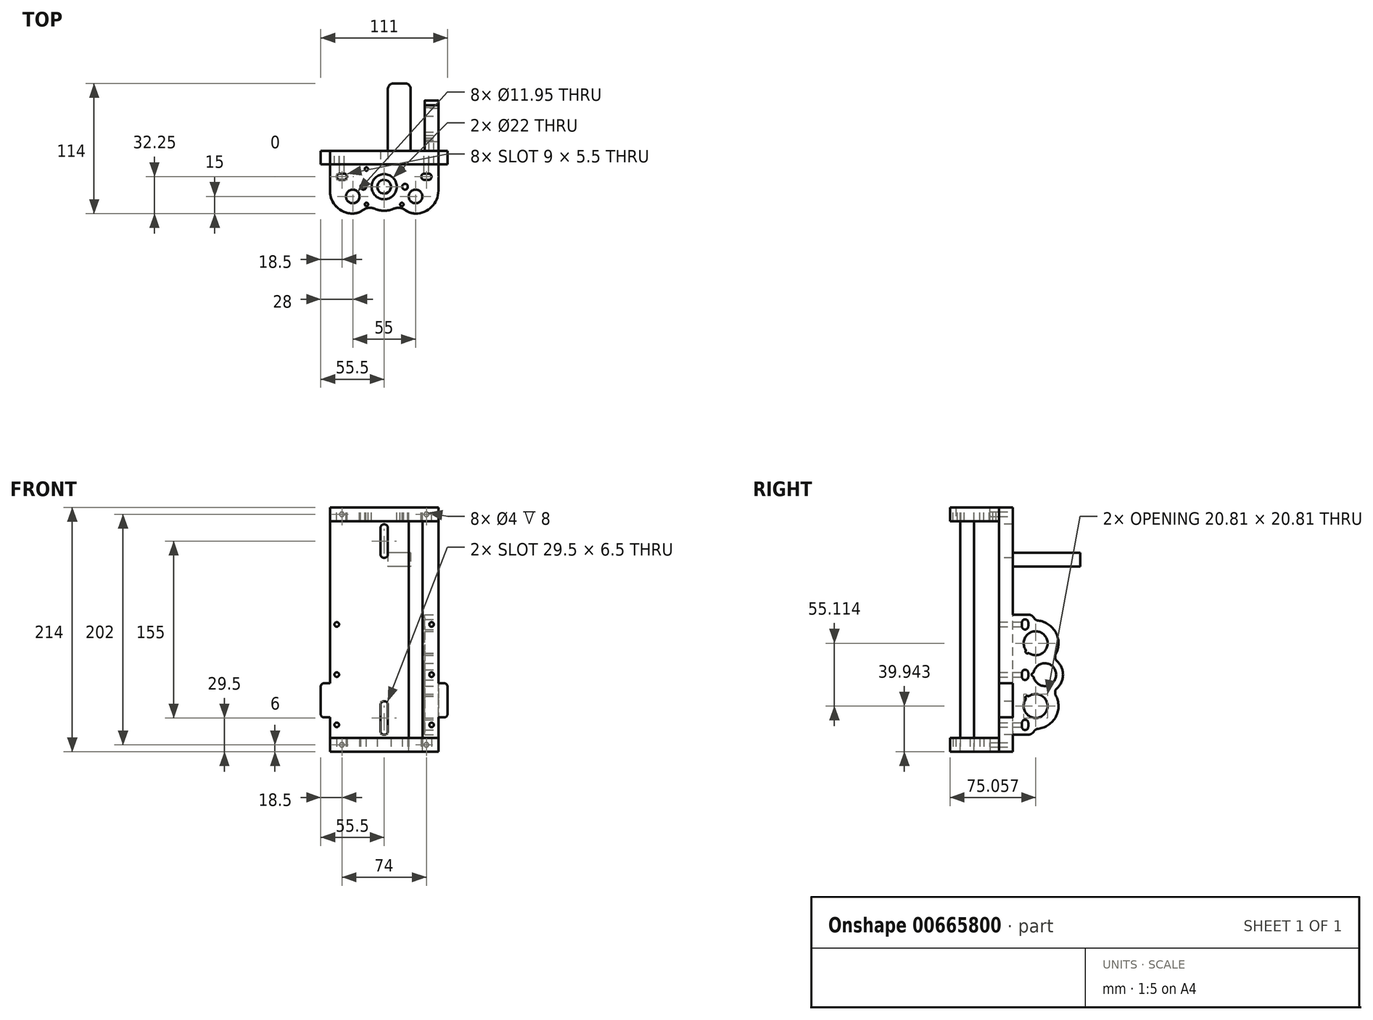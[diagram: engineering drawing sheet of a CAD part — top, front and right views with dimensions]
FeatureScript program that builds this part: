
annotation { "Feature Type Name" : "Feature", "Feature Type Description" : "" }
export const myFeature = defineFeature(function(context is Context, id is Id, definition is map)
    precondition{}
    {
        {
            assignVariable(context, id + "F0", {"name" : "L", "anyValue" : 214});
        }
        {
            var Q0;
            Q0=qCreatedBy(makeId("Front.planeOp"),FACE);
            var sketch = newSketch(context, id + "F1", { "sketchPlane" : qUnion([Q0])});
            skLineSegment(sketch, "E0.bottom", {"start": v(47.5, 0) * mm, "end": v(-47.5, 0) * mm});
            skLineSegment(sketch, "E0.top", {"start": v(-47.5, 214) * mm, "end": v(47.5, 214) * mm});
            skLineSegment(sketch, "E0.left", {"start": v(-47.5, 0) * mm, "end": v(-47.5, 214) * mm});
            skLineSegment(sketch, "E0.right", {"start": v(47.5, 0) * mm, "end": v(47.5, 214) * mm});
            skLineSegment(sketch, "E1.left", {"start": v(3.25, 196) * mm, "end": v(3.25, 173) * mm});
            skLineSegment(sketch, "E1.right", {"start": v(-3.25, 196) * mm, "end": v(-3.25, 173) * mm});
            skArc(sketch, "E2", {"start": v(3.25, 196) * mm, "mid": v(0, 199.25) * mm, "end": v(-3.25, 196) * mm});
            skArc(sketch, "E3", {"start": v(-3.25, 173) * mm, "mid": v(0, 169.75) * mm, "end": v(3.25, 173) * mm});
            skLineSegment(sketch, "E4", {"start": v(0, 214) * mm, "end": v(0, 196) * mm, "construction": true});
            skLineSegment(sketch, "E5.left", {"start": v(-3.25, 18) * mm, "end": v(-3.25, 41) * mm});
            skLineSegment(sketch, "E5.right", {"start": v(3.25, 18) * mm, "end": v(3.25, 41) * mm});
            skArc(sketch, "E6", {"start": v(-3.25, 18) * mm, "mid": v(0, 14.75) * mm, "end": v(3.25, 18) * mm});
            skArc(sketch, "E7", {"start": v(3.25, 41) * mm, "mid": v(0, 44.25) * mm, "end": v(-3.25, 41) * mm});
            skLineSegment(sketch, "E8", {"start": v(0, 0) * mm, "end": v(0, 18) * mm, "construction": true});
            skSolve(sketch);
        }
        {
            var Q0;
            Q0=qSketchRegion(id+"F1",true);
            extrude(context, id + "F2", {"entities" : qUnion([Q0]), "oppositeDirection" : true, "depth" : 12 * mm, "offsetDistance" : 25 * mm});
        }
        {
            var Q0;
            Q0=makeQuery(id+"F2.opExtrude","SWEPT_FACE",FACE,{"disambiguationData":[OSD([sQuery(id+"F1.wireOp",EDGE,"E0.top")])]});
            var sketch = newSketch(context, id + "F3", { "sketchPlane" : qUnion([Q0])});
            skLineSegment(sketch, "E9.bottom", {"start": v(-47.5, 0) * mm, "end": v(47.5, 0) * mm});
            skLineSegment(sketch, "E9.top", {"start": v(-27.5, -43) * mm, "end": v(27.5, -43) * mm, "construction": true});
            skLineSegment(sketch, "E9.left", {"start": v(-47.5, 0) * mm, "end": v(-47.5, -23) * mm});
            skLineSegment(sketch, "E9.right", {"start": v(47.5, 0) * mm, "end": v(47.5, -23) * mm});
            skLineSegment(sketch, "E10", {"start": v(0, 0) * mm, "end": v(0, -43) * mm, "construction": true});
            skCircle(sketch, "E11", {"center": v(-27.5, -28) * mm, "radius": 5.97 * mm});
            skCircle(sketch, "E12.MirrorC", {"center": v(27.5, -28) * mm, "radius": 5.97 * mm});
            skArc(sketch, "E13.filletArc", {"start": v(-47.5, -23) * mm, "mid": v(-41.64, -37.14) * mm, "end": v(-27.5, -43) * mm});
            skPoint(sketch, "E14.visualSharp", {"position": v(47.5, -43) * mm});
            skArc(sketch, "E14.filletArc", {"start": v(27.5, -43) * mm, "mid": v(41.64, -37.14) * mm, "end": v(47.5, -23) * mm});
            skCircle(sketch, "E15", {"center": v(0, -19.5) * mm, "radius": 11 * mm});
            skCircle(sketch, "E16", {"center": v(-18.25, -19.5) * mm, "radius": 2.5 * mm});
            skCircle(sketch, "E17.MirrorC", {"center": v(18.25, -19.5) * mm, "radius": 2.5 * mm});
            skLineSegment(sketch, "E18.bottom", {"start": v(-38.75, -8) * mm, "end": v(-35.25, -8) * mm});
            skLineSegment(sketch, "E18.top", {"start": v(-38.75, -13.5) * mm, "end": v(-35.25, -13.5) * mm});
            skArc(sketch, "E19", {"start": v(-38.75, -8) * mm, "mid": v(-41.5, -10.75) * mm, "end": v(-38.75, -13.5) * mm});
            skArc(sketch, "E20", {"start": v(-35.25, -13.5) * mm, "mid": v(-32.5, -10.75) * mm, "end": v(-35.25, -8) * mm});
            skLineSegment(sketch, "E21", {"start": v(-37, -8) * mm, "end": v(-37, -13.5) * mm, "construction": true});
            skArc(sketch, "E22.MirrorCS", {"start": v(35.25, -13.5) * mm, "mid": v(32.5, -10.75) * mm, "end": v(35.25, -8) * mm});
            skLineSegment(sketch, "E23.MirrorCS", {"start": v(38.75, -13.5) * mm, "end": v(35.25, -13.5) * mm});
            skLineSegment(sketch, "E24.MirrorCS", {"start": v(38.75, -8) * mm, "end": v(35.25, -8) * mm});
            skArc(sketch, "E25.MirrorCS", {"start": v(38.75, -8) * mm, "mid": v(41.5, -10.75) * mm, "end": v(38.75, -13.5) * mm});
            skArc(sketch, "E26", {"start": v(-7.8, 0) * mm, "mid": v(0, -40.5) * mm, "end": v(7.8, 0) * mm});
            skCircle(sketch, "E27", {"center": v(-27.5, -28) * mm, "radius": 15 * mm});
            skCircle(sketch, "E28", {"center": v(27.5, -28) * mm, "radius": 15 * mm});
            skSolve(sketch);
        }
        {
            var Q0;
            Q0=qSketchRegion(id+"F3",true);
            extrude(context, id + "F4", {"entities" : qUnion([Q0]), "oppositeDirection" : true, "depth" : 12 * mm, "offsetDistance" : 25 * mm});
        }
        {
            var Q0;
            Q0=makeQuery(id+"F4.opExtrude","SWEPT_EDGE",EDGE,{"disambiguationData":[OSD([sQuery(id+"F3.wireOp",EDGE,"E26"),sQuery(id+"F3.wireOp",EDGE,"E27")])]});
            var Q1;
            Q1=makeQuery(id+"F4.opExtrude","SWEPT_EDGE",EDGE,{"disambiguationData":[OSD([sQuery(id+"F3.wireOp",EDGE,"E26"),sQuery(id+"F3.wireOp",EDGE,"E28")])]});
            fillet(context, id + "F5", {"entities" : qUnion([Q0, Q1]), "radius" : 10 * mm, "tangentPropagation" : true, "allowEdgeOverflow" : false});
        }
        {
            var Q0;
            Q0=makeQuery(id+"F4.opExtrude","CAP_FACE",FACE,{"disambiguationData":[OSD([sQuery(id+"F3.wireOp",EDGE,"E9.bottom"),sQuery(id+"F3.wireOp",EDGE,"E9.top"),sQuery(id+"F3.wireOp",EDGE,"E9.left"),sQuery(id+"F3.wireOp",EDGE,"E9.right"),sQuery(id+"F3.wireOp",EDGE,"E11"),sQuery(id+"F3.wireOp",EDGE,"E12.MirrorC"),sQuery(id+"F3.wireOp",EDGE,"E13.filletArc"),sQuery(id+"F3.wireOp",EDGE,"E14.filletArc")])],"isStart":true});
            var sketch = newSketch(context, id + "F6", { "sketchPlane" : qUnion([Q0])});
            skCircle(sketch, "E29", {"center": v(27.5, -28) * mm, "radius": 6 * mm});
            skSolve(sketch);
        }
        {
            var Q0;
            Q0=qSketchRegion(id+"F6",true);
            extrude(context, id + "F7", {"entities" : qUnion([Q0]), "oppositeDirection" : true, "depth" : (getVariable(context, 'L')) * mm, "offsetDistance" : 25 * mm});
        }
        {
            var Q0;
            Q0=makeQuery(id+"F2.opExtrude","SWEPT_FACE",FACE,{"disambiguationData":[OSD([sQuery(id+"F1.wireOp",EDGE,"E0.right")])]});
            var sketch = newSketch(context, id + "F8", { "sketchPlane" : qUnion([Q0])});
            skLineSegment(sketch, "E30.top", {"start": v(52, 40) * mm, "end": v(52, 67.5) * mm, "construction": true});
            skLineSegment(sketch, "E31", {"start": v(12, 67.5) * mm, "end": v(52, 67.5) * mm, "construction": true});
            skPoint(sketch, "E32.centerSnap0", {"position": v(32, 67.5) * mm});
            skArc(sketch, "E33.filletArc", {"start": v(32, 20) * mm, "mid": v(46.14, 25.86) * mm, "end": v(52, 40) * mm});
            skArc(sketch, "E34.filletArc", {"start": v(52, 95) * mm, "mid": v(46.14, 109.14) * mm, "end": v(32, 115) * mm});
            skArc(sketch, "E35", {"start": v(23.22, 45.7) * mm, "mid": v(39.4, 32.6) * mm, "end": v(26.3, 48.78) * mm});
            skArc(sketch, "E36.MirrorC", {"start": v(23.22, 89.3) * mm, "mid": v(39.4, 102.4) * mm, "end": v(26.3, 86.22) * mm});
            skArc(sketch, "E37", {"start": v(47.07, 53.15) * mm, "mid": v(56, 67.5) * mm, "end": v(47.07, 81.85) * mm});
            skArc(sketch, "E38", {"start": v(30.26, 65.33) * mm, "mid": v(49.98, 67.5) * mm, "end": v(30.26, 69.67) * mm});
            skLineSegment(sketch, "E39.bottom", {"start": v(32, 20) * mm, "end": v(28.5, 15) * mm});
            skLineSegment(sketch, "E39.right", {"start": v(28.5, 15) * mm, "end": v(12, 15) * mm});
            skLineSegment(sketch, "E40.bottom", {"start": v(25.5, 25.25) * mm, "end": v(25.5, 21.75) * mm});
            skLineSegment(sketch, "E40.top", {"start": v(20, 25.25) * mm, "end": v(20, 21.75) * mm});
            skArc(sketch, "E41", {"start": v(25.5, 25.25) * mm, "mid": v(22.75, 28) * mm, "end": v(20, 25.25) * mm});
            skArc(sketch, "E42", {"start": v(20, 21.75) * mm, "mid": v(22.75, 19) * mm, "end": v(25.5, 21.75) * mm});
            skLineSegment(sketch, "E43.MirrorCS", {"start": v(32, 115) * mm, "end": v(28.5, 120) * mm});
            skLineSegment(sketch, "E44.MirrorCS", {"start": v(28.5, 120) * mm, "end": v(12, 120) * mm});
            skLineSegment(sketch, "E45.top", {"start": v(20, 69.07) * mm, "end": v(20, 65.57) * mm});
            skArc(sketch, "E46", {"start": v(25.5, 69.07) * mm, "mid": v(22.75, 71.82) * mm, "end": v(20, 69.07) * mm});
            skArc(sketch, "E47", {"start": v(20, 65.57) * mm, "mid": v(22.75, 62.82) * mm, "end": v(25.5, 65.57) * mm});
            skLineSegment(sketch, "E48", {"start": v(20, 23.5) * mm, "end": v(25.5, 23.5) * mm, "construction": true});
            skLineSegment(sketch, "E49.trimOffspring", {"start": v(52, 67.5) * mm, "end": v(52, 95) * mm, "construction": true});
            skLineSegment(sketch, "E50", {"start": v(12, 120) * mm, "end": v(12, 15) * mm});
            skLineSegment(sketch, "E51", {"start": v(32, 40) * mm, "end": v(32, 20) * mm, "construction": true});
            skLineSegment(sketch, "E52", {"start": v(32, 95) * mm, "end": v(32, 40) * mm, "construction": true});
            skArc(sketch, "E53", {"start": v(52, 40) * mm, "mid": v(50.73, 47.02) * mm, "end": v(47.07, 53.15) * mm});
            skArc(sketch, "E54.MirrorCS", {"start": v(52, 95) * mm, "mid": v(50.73, 87.98) * mm, "end": v(47.07, 81.85) * mm});
            skLineSegment(sketch, "E55", {"start": v(32, 95) * mm, "end": v(24.6, 87.6) * mm, "construction": true});
            skArc(sketch, "E56", {"start": v(23.26, 88.29) * mm, "mid": v(23.53, 86.53) * mm, "end": v(25.29, 86.26) * mm});
            skPoint(sketch, "E57.visualSharp", {"position": v(23.61, 88.73) * mm});
            skArc(sketch, "E57.filletArc", {"start": v(23.26, 88.29) * mm, "mid": v(23.38, 88.8) * mm, "end": v(23.22, 89.3) * mm});
            skPoint(sketch, "E58.visualSharp", {"position": v(25.73, 86.61) * mm});
            skArc(sketch, "E58.filletArc", {"start": v(26.3, 86.22) * mm, "mid": v(25.8, 86.38) * mm, "end": v(25.29, 86.26) * mm});
            skArc(sketch, "E59.MirrorCS", {"start": v(26.3, 48.78) * mm, "mid": v(25.8, 48.62) * mm, "end": v(25.29, 48.74) * mm});
            skArc(sketch, "E60.MirrorCS", {"start": v(23.26, 46.71) * mm, "mid": v(23.53, 48.47) * mm, "end": v(25.29, 48.74) * mm});
            skArc(sketch, "E61.MirrorCS", {"start": v(23.26, 46.71) * mm, "mid": v(23.38, 46.2) * mm, "end": v(23.22, 45.7) * mm});
            skLineSegment(sketch, "E62", {"start": v(25.5, 69.07) * mm, "end": v(25.5, 65.57) * mm});
            skArc(sketch, "E63.MirrorCS", {"start": v(25.5, 109.75) * mm, "mid": v(22.75, 107) * mm, "end": v(20, 109.75) * mm});
            skLineSegment(sketch, "E64.MirrorCS", {"start": v(25.5, 109.75) * mm, "end": v(25.5, 113.25) * mm});
            skLineSegment(sketch, "E65.MirrorCS", {"start": v(20, 109.75) * mm, "end": v(20, 113.25) * mm});
            skArc(sketch, "E66.MirrorCS", {"start": v(20, 113.25) * mm, "mid": v(22.75, 116) * mm, "end": v(25.5, 113.25) * mm});
            skArc(sketch, "E67", {"start": v(29.58, 68.93) * mm, "mid": v(28.53, 67.5) * mm, "end": v(29.58, 66.07) * mm});
            skPoint(sketch, "E68.visualSharp", {"position": v(30.14, 69) * mm});
            skArc(sketch, "E68.filletArc", {"start": v(29.58, 68.93) * mm, "mid": v(30.02, 69.21) * mm, "end": v(30.26, 69.67) * mm});
            skPoint(sketch, "E69.visualSharp", {"position": v(30.14, 66) * mm});
            skArc(sketch, "E69.filletArc", {"start": v(30.26, 65.33) * mm, "mid": v(30.02, 65.79) * mm, "end": v(29.58, 66.07) * mm});
            skSolve(sketch);
        }
        {
            var Q0;
            Q0=qSketchRegion(id+"F8",true);
            extrude(context, id + "F9", {"entities" : qUnion([Q0]), "oppositeDirection" : true, "depth" : 12 * mm, "offsetDistance" : 25 * mm});
        }
        {
            var Q0;
            Q0=makeQuery(id+"F2.opExtrude","SWEPT_FACE",FACE,{"disambiguationData":[OSD([sQuery(id+"F1.wireOp",EDGE,"E0.bottom")])]});
            var sketch = newSketch(context, id + "F10", { "sketchPlane" : qUnion([Q0])});
            skLineSegment(sketch, "E70.0", {"start": v(-47.5, 0) * mm, "end": v(47.5, 0) * mm});
            skArc(sketch, "E70.1", {"start": v(47.5, 23) * mm, "mid": v(41.64, 37.14) * mm, "end": v(27.5, 43) * mm});
            skLineSegment(sketch, "E70.3", {"start": v(47.5, 0) * mm, "end": v(47.5, 23) * mm});
            skArc(sketch, "E70.4", {"start": v(-27.5, 43) * mm, "mid": v(-41.64, 37.14) * mm, "end": v(-47.5, 23) * mm});
            skLineSegment(sketch, "E70.5", {"start": v(-47.5, 23) * mm, "end": v(-47.5, 0) * mm});
            skCircle(sketch, "E71.0", {"center": v(-27.5, 28) * mm, "radius": 5.97 * mm});
            skCircle(sketch, "E72.0", {"center": v(27.5, 28) * mm, "radius": 5.97 * mm});
            skCircle(sketch, "E73.0", {"center": v(-18.25, 19.5) * mm, "radius": 2.5 * mm});
            skCircle(sketch, "E74.0", {"center": v(18.25, 19.5) * mm, "radius": 2.5 * mm});
            skCircle(sketch, "E75.0", {"center": v(0, 19.5) * mm, "radius": 6 * mm});
            skArc(sketch, "E76.0", {"start": v(18.43, 39.95) * mm, "mid": v(22.72, 42.22) * mm, "end": v(27.5, 43) * mm});
            skArc(sketch, "E76.1", {"start": v(-27.5, 43) * mm, "mid": v(-22.72, 42.22) * mm, "end": v(-18.43, 39.95) * mm});
            skArc(sketch, "E76.2", {"start": v(-18.43, 39.95) * mm, "mid": v(-13.58, 37.99) * mm, "end": v(-8.4, 38.75) * mm});
            skArc(sketch, "E76.3", {"start": v(-8.4, 38.75) * mm, "mid": v(0, 40.5) * mm, "end": v(8.4, 38.75) * mm});
            skArc(sketch, "E76.4", {"start": v(8.4, 38.75) * mm, "mid": v(13.58, 37.99) * mm, "end": v(18.43, 39.95) * mm});
            skArc(sketch, "E77.0", {"start": v(-38.75, 8) * mm, "mid": v(-41.5, 10.75) * mm, "end": v(-38.75, 13.5) * mm});
            skLineSegment(sketch, "E77.1", {"start": v(-38.75, 8) * mm, "end": v(-35.25, 8) * mm});
            skArc(sketch, "E77.2", {"start": v(-35.25, 13.5) * mm, "mid": v(-32.5, 10.75) * mm, "end": v(-35.25, 8) * mm});
            skLineSegment(sketch, "E77.3", {"start": v(-38.75, 13.5) * mm, "end": v(-35.25, 13.5) * mm});
            skArc(sketch, "E78.0", {"start": v(35.25, 13.5) * mm, "mid": v(32.5, 10.75) * mm, "end": v(35.25, 8) * mm});
            skLineSegment(sketch, "E78.1", {"start": v(38.75, 13.5) * mm, "end": v(35.25, 13.5) * mm});
            skArc(sketch, "E78.2", {"start": v(38.75, 8) * mm, "mid": v(41.5, 10.75) * mm, "end": v(38.75, 13.5) * mm});
            skLineSegment(sketch, "E78.3", {"start": v(38.75, 8) * mm, "end": v(35.25, 8) * mm});
            skSolve(sketch);
        }
        {
            var Q0;
            Q0=qSketchRegion(id+"F10",true);
            extrude(context, id + "F11", {"entities" : qUnion([Q0]), "oppositeDirection" : true, "depth" : 12 * mm, "offsetDistance" : 25 * mm});
        }
        {
            var Q0;
            Q0=makeQuery(id+"F2.opExtrude","CAP_FACE",FACE,{"disambiguationData":[OSD([sQuery(id+"F1.wireOp",EDGE,"E0.bottom"),sQuery(id+"F1.wireOp",EDGE,"E0.top"),sQuery(id+"F1.wireOp",EDGE,"E0.left"),sQuery(id+"F1.wireOp",EDGE,"E0.right")])],"isStart":false});
            var sketch = newSketch(context, id + "F12", { "sketchPlane" : qUnion([Q0])});
            skCircle(sketch, "E79", {"center": v(-37, 208) * mm, "radius": 2 * mm});
            skCircle(sketch, "E80", {"center": v(37, 208) * mm, "radius": 2 * mm});
            skLineSegment(sketch, "E81", {"start": v(-47.5, 107) * mm, "end": v(47.5, 107) * mm, "construction": true});
            skCircle(sketch, "E82.MirrorC", {"center": v(37, 6) * mm, "radius": 2 * mm});
            skCircle(sketch, "E83.MirrorC", {"center": v(-37, 6) * mm, "radius": 2 * mm});
            skCircle(sketch, "E84", {"center": v(-41.5, 23.5) * mm, "radius": 2 * mm});
            skCircle(sketch, "E85", {"center": v(-41.5, 111.5) * mm, "radius": 2 * mm});
            skCircle(sketch, "E86", {"center": v(-41.5, 67.5) * mm, "radius": 2 * mm});
            skLineSegment(sketch, "E87", {"start": v(0, 107) * mm, "end": v(0, 0) * mm, "construction": true});
            skCircle(sketch, "E88.MirrorC", {"center": v(41.5, 23.5) * mm, "radius": 2 * mm});
            skCircle(sketch, "E89.MirrorC", {"center": v(41.5, 111.5) * mm, "radius": 2 * mm});
            skCircle(sketch, "E90.MirrorC", {"center": v(41.5, 67.5) * mm, "radius": 2 * mm});
            skSolve(sketch);
        }
        {
            var Q0;
            Q0=qSketchRegion(id+"F12",true);
            extrude(context, id + "F13", {"entities" : qUnion([Q0]), "operationType" : NewBodyOperationType.REMOVE, "oppositeDirection" : true, "depth" : 25 * mm, "offsetDistance" : 25 * mm, "hasSecondDirection" : true, "secondDirectionOppositeDirection" : false, "secondDirectionDepth" : 10 * mm});
        }
        {
            var Q0;
            Q0=makeQuery(id+"F4.opExtrude","CAP_FACE",FACE,{"disambiguationData":[OSD([sQuery(id+"F3.wireOp",EDGE,"E9.bottom"),sQuery(id+"F3.wireOp",EDGE,"E9.left"),sQuery(id+"F3.wireOp",EDGE,"E9.right"),sQuery(id+"F3.wireOp",EDGE,"E11"),sQuery(id+"F3.wireOp",EDGE,"E12.MirrorC"),sQuery(id+"F3.wireOp",EDGE,"E13.filletArc"),sQuery(id+"F3.wireOp",EDGE,"E14.filletArc"),sQuery(id+"F3.wireOp",EDGE,"E15"),sQuery(id+"F3.wireOp",EDGE,"E16"),sQuery(id+"F3.wireOp",EDGE,"E17.MirrorC"),sQuery(id+"F3.wireOp",EDGE,"E18.bottom"),sQuery(id+"F3.wireOp",EDGE,"E18.top"),sQuery(id+"F3.wireOp",EDGE,"E19"),sQuery(id+"F3.wireOp",EDGE,"E20"),sQuery(id+"F3.wireOp",EDGE,"E22.MirrorCS"),sQuery(id+"F3.wireOp",EDGE,"E23.MirrorCS"),sQuery(id+"F3.wireOp",EDGE,"E24.MirrorCS"),sQuery(id+"F3.wireOp",EDGE,"E25.MirrorCS"),sQuery(id+"F3.wireOp",EDGE,"E26"),sQuery(id+"F3.wireOp",EDGE,"E27"),sQuery(id+"F3.wireOp",EDGE,"E28")])],"isStart":true});
            var sketch = newSketch(context, id + "F14", { "sketchPlane" : qUnion([Q0])});
            skLineSegment(sketch, "E91.bottom", {"start": v(-15.5, -4) * mm, "end": v(15.5, -4) * mm, "construction": true});
            skLineSegment(sketch, "E91.top", {"start": v(-15.5, -35) * mm, "end": v(15.5, -35) * mm, "construction": true});
            skLineSegment(sketch, "E91.left", {"start": v(-15.5, -4) * mm, "end": v(-15.5, -35) * mm, "construction": true});
            skLineSegment(sketch, "E91.right", {"start": v(15.5, -4) * mm, "end": v(15.5, -35) * mm, "construction": true});
            skLineSegment(sketch, "E92", {"start": v(-15.5, -19.5) * mm, "end": v(15.5, -19.5) * mm, "construction": true});
            skPoint(sketch, "E93", {"position": v(0, -19.5) * mm});
            skCircle(sketch, "E94", {"center": v(-15.5, -4) * mm, "radius": 1.5 * mm});
            skCircle(sketch, "E95.1.0", {"center": v(-15.5, -35) * mm, "radius": 1.5 * mm});
            skCircle(sketch, "E95.2.0", {"center": v(15.5, -35) * mm, "radius": 1.5 * mm});
            skCircle(sketch, "E95.3.0", {"center": v(15.5, -4) * mm, "radius": 1.5 * mm});
            skLineSegment(sketch, "E96", {"start": v(-15.5, -4) * mm, "end": v(15.5, -35) * mm, "construction": true});
            skSolve(sketch);
        }
        {
            var Q0;
            Q0=qSketchRegion(id+"F14",true);
            extrude(context, id + "F15", {"entities" : qUnion([Q0]), "operationType" : NewBodyOperationType.REMOVE, "oppositeDirection" : true, "depth" : 25 * mm, "offsetDistance" : 25 * mm});
        }
        {
            var Q0;
            Q0=makeQuery(id+"F9.opExtrude","SWEPT_EDGE",EDGE,{"disambiguationData":[OSD([sQuery(id+"F8.wireOp",EDGE,"E33.filletArc"),sQuery(id+"F8.wireOp",EDGE,"E39.bottom")])]});
            var Q1;
            Q1=makeQuery(id+"F9.opExtrude","SWEPT_EDGE",EDGE,{"disambiguationData":[OSD([sQuery(id+"F8.wireOp",EDGE,"E39.bottom"),sQuery(id+"F8.wireOp",EDGE,"E39.right")])]});
            var Q2;
            Q2=makeQuery(id+"F9.opExtrude","SWEPT_EDGE",EDGE,{"disambiguationData":[OSD([sQuery(id+"F8.wireOp",EDGE,"E34.filletArc"),sQuery(id+"F8.wireOp",EDGE,"E43.MirrorCS")])]});
            var Q3;
            Q3=makeQuery(id+"F9.opExtrude","SWEPT_EDGE",EDGE,{"disambiguationData":[OSD([sQuery(id+"F8.wireOp",EDGE,"E43.MirrorCS"),sQuery(id+"F8.wireOp",EDGE,"E44.MirrorCS")])]});
            fillet(context, id + "F16", {"entities" : qUnion([Q0, Q1, Q2, Q3]), "radius" : 5 * mm, "tangentPropagation" : true, "allowEdgeOverflow" : false});
        }
        {
            var Q0;
            Q0=makeQuery(id+"F9.opExtrude","SWEPT_EDGE",EDGE,{"disambiguationData":[OSD([sQuery(id+"F8.wireOp",EDGE,"E37"),sQuery(id+"F8.wireOp",EDGE,"E54.MirrorCS")])]});
            var Q1;
            Q1=makeQuery(id+"F9.opExtrude","SWEPT_EDGE",EDGE,{"disambiguationData":[OSD([sQuery(id+"F8.wireOp",EDGE,"E37"),sQuery(id+"F8.wireOp",EDGE,"E53")])]});
            var Q2;
            Q2=makeQuery(id+"F9.opExtrude","SWEPT_EDGE",EDGE,{"disambiguationData":[OSD([sQuery(id+"F8.wireOp",EDGE,"E38"),sQuery(id+"F8.wireOp",EDGE,"E45.bottom"),sQuery(id+"F8.wireOp",EDGE,"E46")])]});
            var Q3;
            Q3=makeQuery(id+"F9.opExtrude","SWEPT_EDGE",EDGE,{"disambiguationData":[OSD([sQuery(id+"F8.wireOp",EDGE,"E38"),sQuery(id+"F8.wireOp",EDGE,"E45.bottom"),sQuery(id+"F8.wireOp",EDGE,"E47")])]});
            fillet(context, id + "F17", {"entities" : qUnion([Q0, Q1, Q2, Q3]), "radius" : 5 * mm, "tangentPropagation" : true, "allowEdgeOverflow" : false});
        }
        {
            var Q0;
            Q0=makeQuery(id+"F2.opExtrude","CAP_FACE",FACE,{"disambiguationData":[OSD([sQuery(id+"F1.wireOp",EDGE,"E0.bottom"),sQuery(id+"F1.wireOp",EDGE,"E0.top"),sQuery(id+"F1.wireOp",EDGE,"E0.left"),sQuery(id+"F1.wireOp",EDGE,"E0.right"),sQuery(id+"F1.wireOp",EDGE,"E1.left"),sQuery(id+"F1.wireOp",EDGE,"E1.right"),sQuery(id+"F1.wireOp",EDGE,"E2"),sQuery(id+"F1.wireOp",EDGE,"E3"),sQuery(id+"F1.wireOp",EDGE,"E5.left"),sQuery(id+"F1.wireOp",EDGE,"E5.right"),sQuery(id+"F1.wireOp",EDGE,"E6"),sQuery(id+"F1.wireOp",EDGE,"E7")])],"isStart":false});
            var sketch = newSketch(context, id + "F18", { "sketchPlane" : qUnion([Q0])});
            skLineSegment(sketch, "E97.bottom", {"start": v(47.5, 30) * mm, "end": v(55.5, 30) * mm});
            skLineSegment(sketch, "E97.top", {"start": v(47.5, 60) * mm, "end": v(55.5, 60) * mm});
            skLineSegment(sketch, "E97.left", {"start": v(47.5, 30) * mm, "end": v(47.5, 60) * mm});
            skLineSegment(sketch, "E97.right", {"start": v(55.5, 30) * mm, "end": v(55.5, 60) * mm});
            skLineSegment(sketch, "E98", {"start": v(0, 18) * mm, "end": v(0, 41) * mm, "construction": true});
            skLineSegment(sketch, "E99.MirrorCS", {"start": v(-47.5, 60) * mm, "end": v(-55.5, 60) * mm});
            skLineSegment(sketch, "E100.MirrorCS", {"start": v(-47.5, 30) * mm, "end": v(-47.5, 60) * mm});
            skLineSegment(sketch, "E101.MirrorCS", {"start": v(-55.5, 30) * mm, "end": v(-55.5, 60) * mm});
            skLineSegment(sketch, "E102.MirrorCS", {"start": v(-47.5, 30) * mm, "end": v(-55.5, 30) * mm});
            skSolve(sketch);
        }
        {
            var Q0;
            Q0 = qSketchRegion(id + "F18", true);
            extrude(context, id + "F19", {"entities" : qUnion([Q0]), "operationType" : NewBodyOperationType.ADD, "oppositeDirection" : true, "depth" : 12 * mm, "offsetDistance" : 25 * mm});
        }
        {
            var Q0;
            Q0=makeQuery(id+"F19.opExtrude","SWEPT_EDGE",EDGE,{"disambiguationData":[OSD([sQuery(id+"F1.wireOp",EDGE,"E0.left"),sQuery(id+"F18.wireOp",EDGE,"E97.top"),sQuery(id+"F18.wireOp",EDGE,"E97.left")])]});
            var Q1;
            Q1=makeQuery(id+"F19.opExtrude","SWEPT_EDGE",EDGE,{"disambiguationData":[OSD([sQuery(id+"F1.wireOp",EDGE,"E0.left"),sQuery(id+"F18.wireOp",EDGE,"E97.bottom"),sQuery(id+"F18.wireOp",EDGE,"E97.left")])]});
            var Q2;
            Q2=makeQuery(id+"F19.opExtrude","SWEPT_EDGE",EDGE,{"disambiguationData":[OSD([sQuery(id+"F18.wireOp",EDGE,"E97.bottom"),sQuery(id+"F18.wireOp",EDGE,"E97.right")])]});
            var Q3;
            Q3=makeQuery(id+"F19.opExtrude","SWEPT_EDGE",EDGE,{"disambiguationData":[OSD([sQuery(id+"F18.wireOp",EDGE,"E97.top"),sQuery(id+"F18.wireOp",EDGE,"E97.right")])]});
            var Q4;
            Q4=makeQuery(id+"F19.opExtrude","SWEPT_EDGE",EDGE,{"disambiguationData":[OSD([sQuery(id+"F18.wireOp",EDGE,"E101.MirrorCS"),sQuery(id+"F18.wireOp",EDGE,"E102.MirrorCS")])]});
            var Q5;
            Q5=makeQuery(id+"F19.opExtrude","SWEPT_EDGE",EDGE,{"disambiguationData":[OSD([sQuery(id+"F1.wireOp",EDGE,"E0.right"),sQuery(id+"F18.wireOp",EDGE,"E100.MirrorCS"),sQuery(id+"F18.wireOp",EDGE,"E102.MirrorCS")])]});
            var Q6;
            Q6=makeQuery(id+"F19.opExtrude","SWEPT_EDGE",EDGE,{"disambiguationData":[OSD([sQuery(id+"F18.wireOp",EDGE,"E99.MirrorCS"),sQuery(id+"F18.wireOp",EDGE,"E101.MirrorCS")])]});
            var Q7;
            Q7=makeQuery(id+"F19.opExtrude","SWEPT_EDGE",EDGE,{"disambiguationData":[OSD([sQuery(id+"F1.wireOp",EDGE,"E0.right"),sQuery(id+"F18.wireOp",EDGE,"E99.MirrorCS"),sQuery(id+"F18.wireOp",EDGE,"E100.MirrorCS")])]});
            fillet(context, id + "F20", {"entities" : qUnion([Q0, Q1, Q2, Q3, Q4, Q5, Q6, Q7]), "radius" : 3 * mm, "tangentPropagation" : true, "allowEdgeOverflow" : false});
        }
        {
            var Q0;
            Q0=makeQuery(id+"F19.boolean.opBoolean","MERGE",FACE,{"derivedFrom":[makeQuery(id+"F2.opExtrude","CAP_FACE",FACE,{"disambiguationData":[OSD([sQuery(id+"F1.wireOp",EDGE,"E0.bottom"),sQuery(id+"F1.wireOp",EDGE,"E0.top"),sQuery(id+"F1.wireOp",EDGE,"E0.left"),sQuery(id+"F1.wireOp",EDGE,"E0.right"),sQuery(id+"F1.wireOp",EDGE,"E1.left"),sQuery(id+"F1.wireOp",EDGE,"E1.right"),sQuery(id+"F1.wireOp",EDGE,"E2"),sQuery(id+"F1.wireOp",EDGE,"E3"),sQuery(id+"F1.wireOp",EDGE,"E5.left"),sQuery(id+"F1.wireOp",EDGE,"E5.right"),sQuery(id+"F1.wireOp",EDGE,"E6"),sQuery(id+"F1.wireOp",EDGE,"E7")])],"isStart":false}),makeQuery(id+"F19.opExtrude","CAP_FACE",FACE,{"disambiguationData":[OSD([sQuery(id+"F18.wireOp",EDGE,"E97.bottom"),sQuery(id+"F18.wireOp",EDGE,"E97.top"),sQuery(id+"F18.wireOp",EDGE,"E97.left"),sQuery(id+"F18.wireOp",EDGE,"E97.right")])],"isStart":true}),makeQuery(id+"F19.opExtrude","CAP_FACE",FACE,{"disambiguationData":[OSD([sQuery(id+"F18.wireOp",EDGE,"E99.MirrorCS"),sQuery(id+"F18.wireOp",EDGE,"E100.MirrorCS"),sQuery(id+"F18.wireOp",EDGE,"E101.MirrorCS"),sQuery(id+"F18.wireOp",EDGE,"E102.MirrorCS")])],"isStart":true})]});
            var sketch = newSketch(context, id + "F21", { "sketchPlane" : qUnion([Q0])});
            skLineSegment(sketch, "E103.bottom", {"start": v(-23.25, 174.2) * mm, "end": v(-3.25, 174.2) * mm});
            skLineSegment(sketch, "E103.top", {"start": v(-23.25, 162.2) * mm, "end": v(-3.25, 162.2) * mm});
            skLineSegment(sketch, "E103.left", {"start": v(-23.25, 174.2) * mm, "end": v(-23.25, 162.2) * mm});
            skLineSegment(sketch, "E103.right", {"start": v(-3.25, 174.2) * mm, "end": v(-3.25, 162.2) * mm});
            skLineSegment(sketch, "E104", {"start": v(0, 174.2) * mm, "end": v(0, 214) * mm, "construction": true});
            skSolve(sketch);
        }
        {
            var Q0;
            Q0 = qSketchRegion(id + "F21", true);
            extrude(context, id + "F22", {"entities" : qUnion([Q0]), "depth" : 59 * mm, "offsetDistance" : 25 * mm});
        }
        {
            var Q0;
            Q0=makeQuery(id+"F22.opExtrude","CAP_EDGE",EDGE,{"disambiguationData":[OSD([sQuery(id+"F21.wireOp",EDGE,"E103.right")])],"isStart":false});
            var Q1;
            Q1=makeQuery(id+"F22.opExtrude","CAP_EDGE",EDGE,{"disambiguationData":[OSD([sQuery(id+"F21.wireOp",EDGE,"E103.left")])],"isStart":false});
            fillet(context, id + "F23", {"entities" : qUnion([Q0, Q1]), "radius" : 5 * mm, "tangentPropagation" : true, "allowEdgeOverflow" : false});
        }
    });
